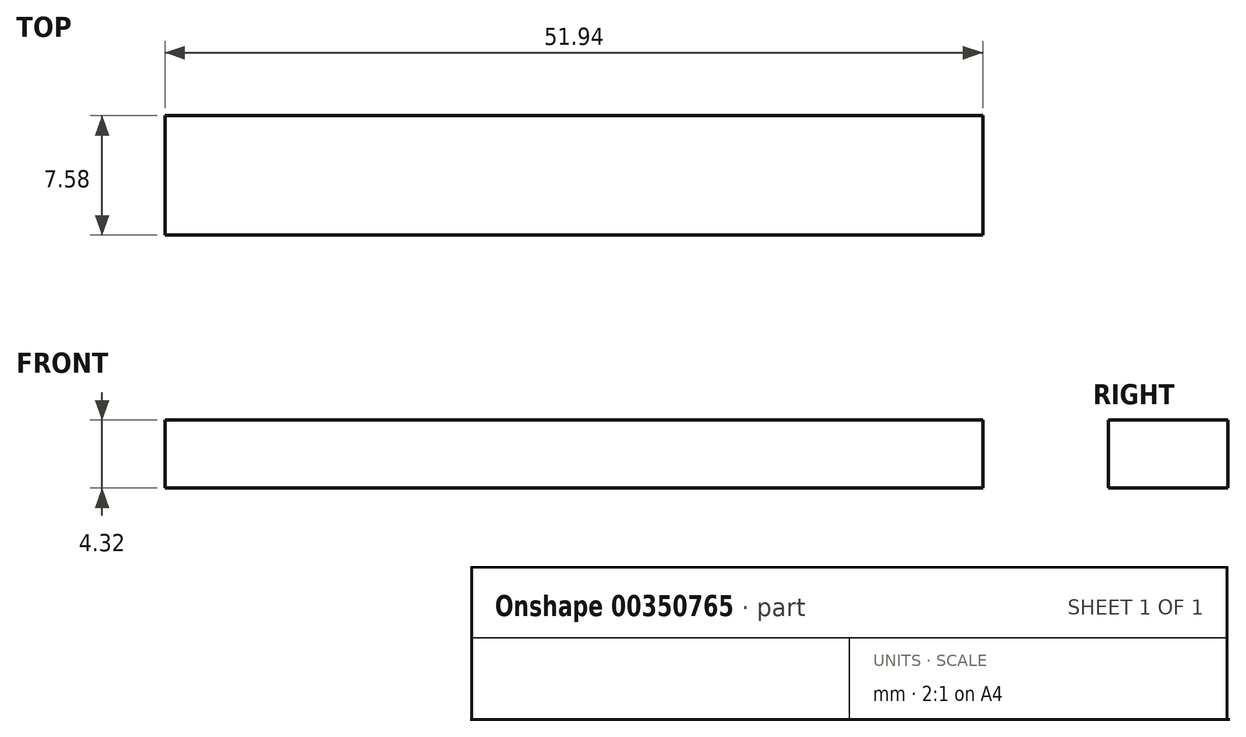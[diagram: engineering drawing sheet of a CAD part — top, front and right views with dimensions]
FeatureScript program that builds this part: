
annotation { "Feature Type Name" : "Feature", "Feature Type Description" : "" }
export const myFeature = defineFeature(function(context is Context, id is Id, definition is map)
    precondition{}
    {
        {
            var Q0;
            Q0=qCreatedBy(makeId("Top.planeOp"),FACE);
            var sketch = newSketch(context, id + "F0", { "sketchPlane" : qUnion([Q0])});
            skLineSegment(sketch, "E0.bottom", {"start": v(25.97, 3.8) * mm, "end": v(-25.97, 3.8) * mm});
            skLineSegment(sketch, "E0.top", {"start": v(25.97, -3.8) * mm, "end": v(-25.97, -3.8) * mm});
            skLineSegment(sketch, "E0.left", {"start": v(25.97, 3.8) * mm, "end": v(25.97, -3.8) * mm});
            skLineSegment(sketch, "E0.right", {"start": v(-25.97, 3.8) * mm, "end": v(-25.97, -3.8) * mm});
            skPoint(sketch, "E0.middle", {"position": v(0, 0) * mm});
            skSolve(sketch);
        }
        {
            var Q0;
            Q0=makeQuery(id+"F0.imprint","IMPRINT",FACE,{"disambiguationData":[TD([[makeQuery(id+"F0.imprint","IMPRINT",EDGE,{"derivedFrom":sQuery(id+"F0.wireOp",EDGE,"E0.bottom")}),1.0]])]});
            extrude(context, id + "F1", {"entities" : qUnion([Q0]), "depth" : 4.32 * mm});
        }
    });
